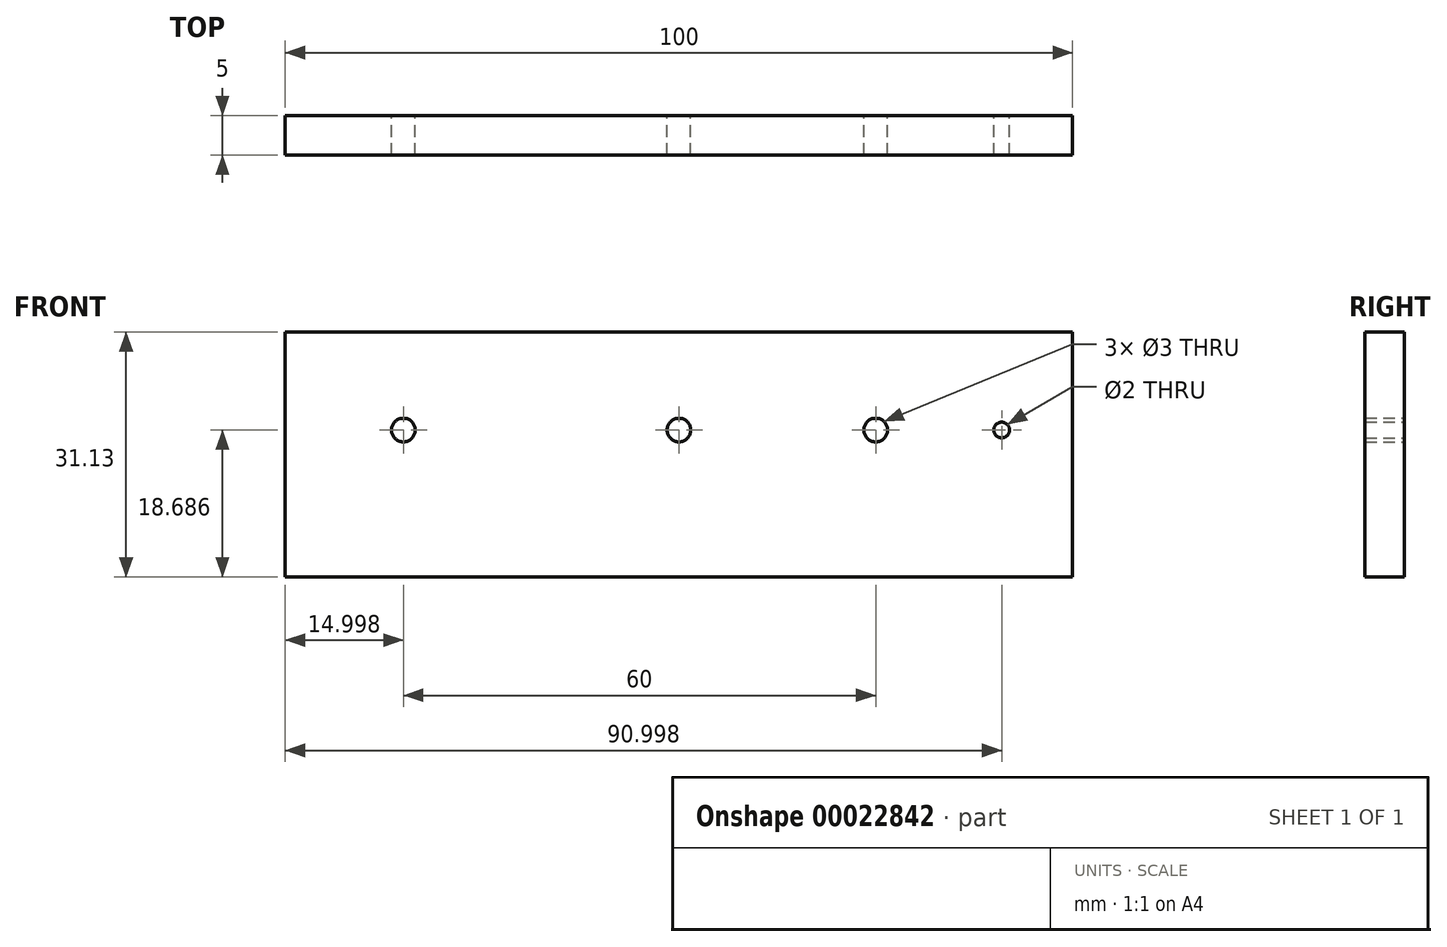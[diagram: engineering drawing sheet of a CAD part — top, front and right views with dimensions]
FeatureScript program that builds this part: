
annotation { "Feature Type Name" : "Feature", "Feature Type Description" : "" }
export const myFeature = defineFeature(function(context is Context, id is Id, definition is map)
    precondition{}
    {
        {
            var Q0;
            Q0=qCreatedBy(makeId("Front.planeOp"),FACE);
            var sketch = newSketch(context, id + "F0", { "sketchPlane" : qUnion([Q0])});
            skLineSegment(sketch, "E0.bottom", {"start": v(-86.38, 57.05) * mm, "end": v(13.62, 57.05) * mm});
            skLineSegment(sketch, "E0.top", {"start": v(-86.38, 25.92) * mm, "end": v(13.62, 25.92) * mm});
            skLineSegment(sketch, "E0.left", {"start": v(-86.38, 57.05) * mm, "end": v(-86.38, 25.92) * mm});
            skLineSegment(sketch, "E0.right", {"start": v(13.62, 57.05) * mm, "end": v(13.62, 25.92) * mm});
            skCircle(sketch, "E1", {"center": v(-71.38, 44.6) * mm, "radius": 1.5 * mm});
            skCircle(sketch, "E2", {"center": v(-36.38, 44.6) * mm, "radius": 1.5 * mm});
            skCircle(sketch, "E3", {"center": v(-11.38, 44.6) * mm, "radius": 1.5 * mm});
            skCircle(sketch, "E4", {"center": v(4.62, 44.6) * mm, "radius": 1 * mm});
            skSolve(sketch);
        }
        {
            var Q0;
            Q0=makeQuery(id+"F0.imprint","IMPRINT",FACE,{"disambiguationData":[TD([[makeQuery(id+"F0.imprint","IMPRINT",EDGE,{"derivedFrom":sQuery(id+"F0.wireOp",EDGE,"E0.bottom")}),-1.0]])]});
            extrude(context, id + "F1", {"entities" : qUnion([Q0]), "depth" : 5 * mm});
        }
    });
